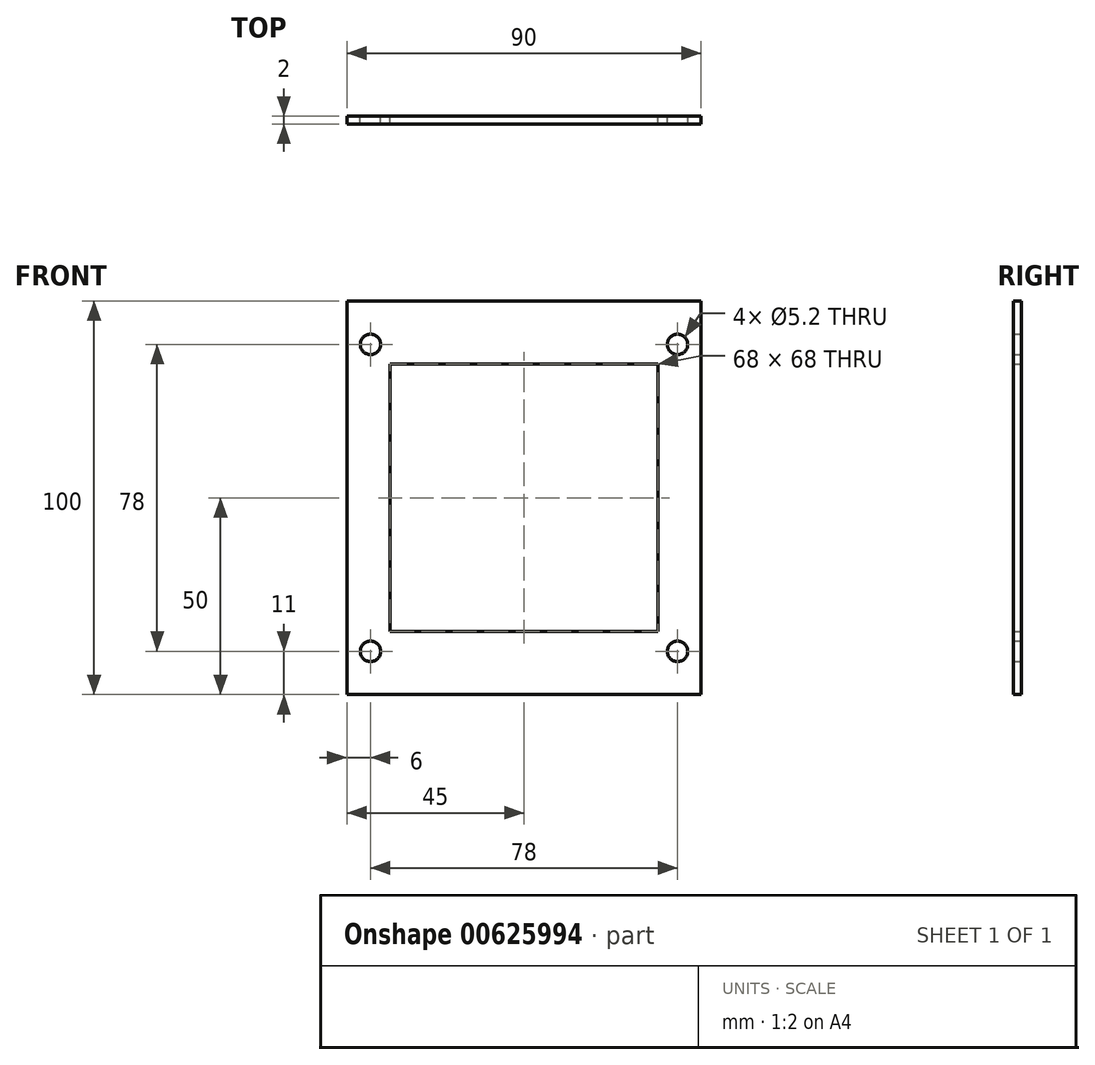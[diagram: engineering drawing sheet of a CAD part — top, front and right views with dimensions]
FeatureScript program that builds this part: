
annotation { "Feature Type Name" : "Feature", "Feature Type Description" : "" }
export const myFeature = defineFeature(function(context is Context, id is Id, definition is map)
    precondition{}
    {
        {
            var Q0;
            Q0=qCreatedBy(makeId("Front.planeOp"),FACE);
            var sketch = newSketch(context, id + "F0", { "sketchPlane" : qUnion([Q0])});
            skLineSegment(sketch, "E0.bottom", {"start": v(-8.75, -16) * mm, "end": v(81.25, -16) * mm});
            skLineSegment(sketch, "E0.top", {"start": v(-8.75, 84) * mm, "end": v(81.25, 84) * mm});
            skLineSegment(sketch, "E0.left", {"start": v(-8.75, -16) * mm, "end": v(-8.75, 84) * mm});
            skLineSegment(sketch, "E0.right", {"start": v(81.25, -16) * mm, "end": v(81.25, 84) * mm});
            skLineSegment(sketch, "E1.bottom", {"start": v(2.25, 68) * mm, "end": v(70.25, 68) * mm});
            skLineSegment(sketch, "E1.top", {"start": v(2.25, 0) * mm, "end": v(70.25, 0) * mm});
            skLineSegment(sketch, "E1.left", {"start": v(2.25, 68) * mm, "end": v(2.25, 0) * mm});
            skLineSegment(sketch, "E1.right", {"start": v(70.25, 68) * mm, "end": v(70.25, 0) * mm});
            skCircle(sketch, "E2", {"center": v(-2.75, 73) * mm, "radius": 2.6 * mm});
            skCircle(sketch, "E3", {"center": v(75.25, 73) * mm, "radius": 2.6 * mm});
            skCircle(sketch, "E4", {"center": v(75.25, -5) * mm, "radius": 2.6 * mm});
            skCircle(sketch, "E5", {"center": v(-2.75, -5) * mm, "radius": 2.6 * mm});
            skSolve(sketch);
        }
        {
            var Q0;
            Q0 = qSketchRegion(id + "F0", true);
            extrude(context, id + "F1", {"entities" : qUnion([Q0]), "depth" : 2 * mm, "offsetDistance" : 25 * mm});
        }
    });
